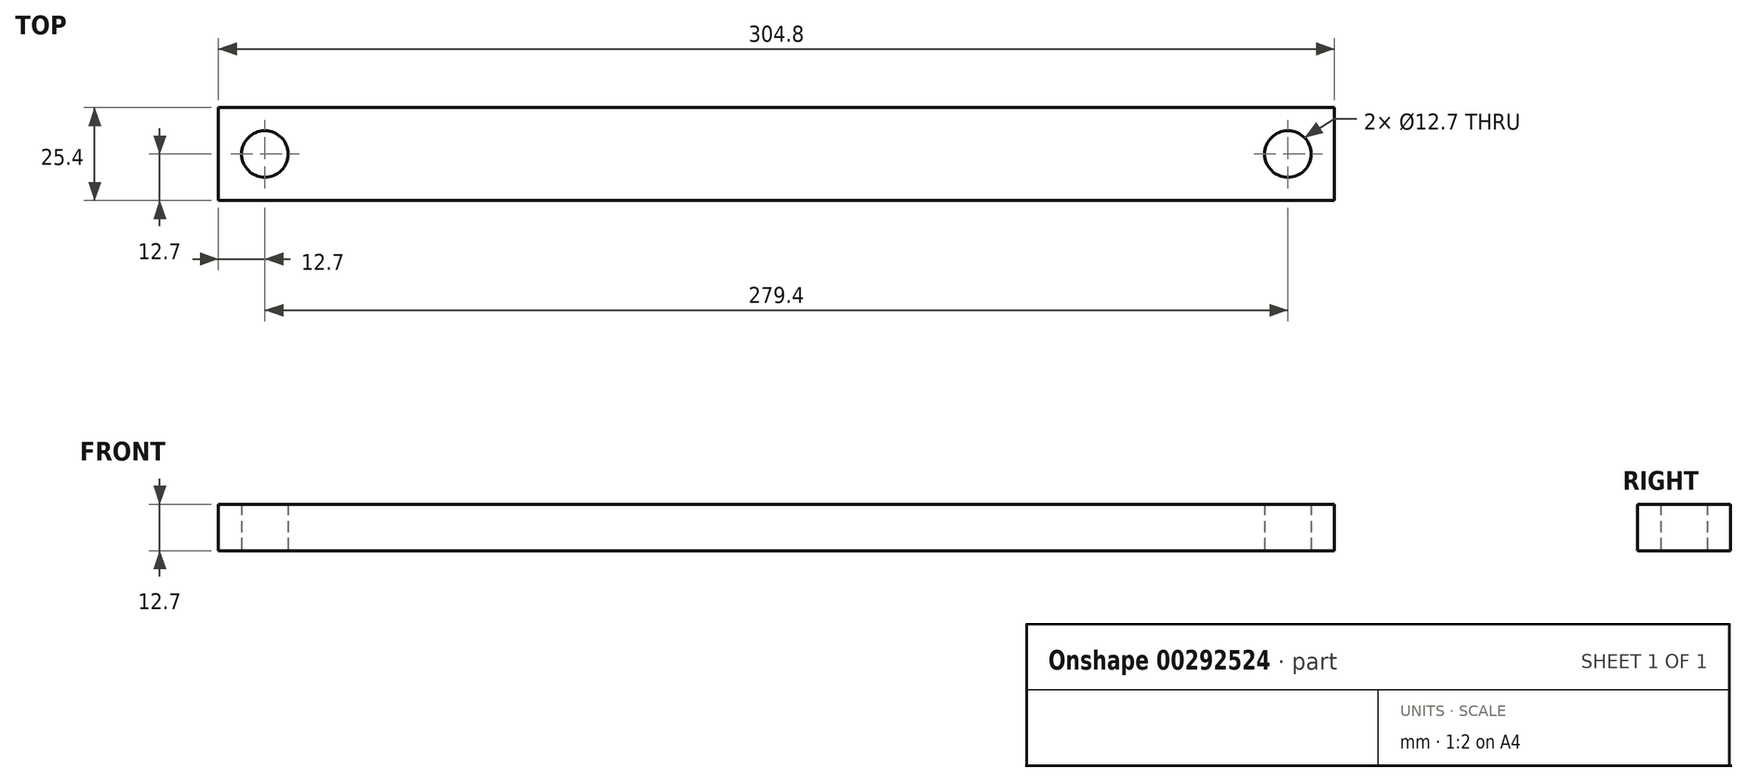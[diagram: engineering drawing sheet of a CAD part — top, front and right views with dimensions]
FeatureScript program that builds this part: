
annotation { "Feature Type Name" : "Feature", "Feature Type Description" : "" }
export const myFeature = defineFeature(function(context is Context, id is Id, definition is map)
    precondition{}
    {
        {
            var Q0;
            Q0=qCreatedBy(makeId("Top.planeOp"),FACE);
            var sketch = newSketch(context, id + "F0", { "sketchPlane" : qUnion([Q0])});
            skLineSegment(sketch, "E0.bottom", {"start": v(0, 0) * mm, "end": v(304.8, 0) * mm});
            skLineSegment(sketch, "E0.top", {"start": v(0, 25.4) * mm, "end": v(304.8, 25.4) * mm});
            skLineSegment(sketch, "E0.left", {"start": v(0, 0) * mm, "end": v(0, 25.4) * mm});
            skLineSegment(sketch, "E0.right", {"start": v(304.8, 0) * mm, "end": v(304.8, 25.4) * mm});
            skCircle(sketch, "E1", {"center": v(12.7, 12.7) * mm, "radius": 6.35 * mm});
            skCircle(sketch, "E2", {"center": v(292.1, 12.7) * mm, "radius": 6.35 * mm});
            skSolve(sketch);
        }
        {
            var Q0;
            Q0 = qSketchRegion(id + "F0", true);
            extrude(context, id + "F1", {"entities" : qUnion([Q0]), "depth" : 12.7 * mm});
        }
    });
